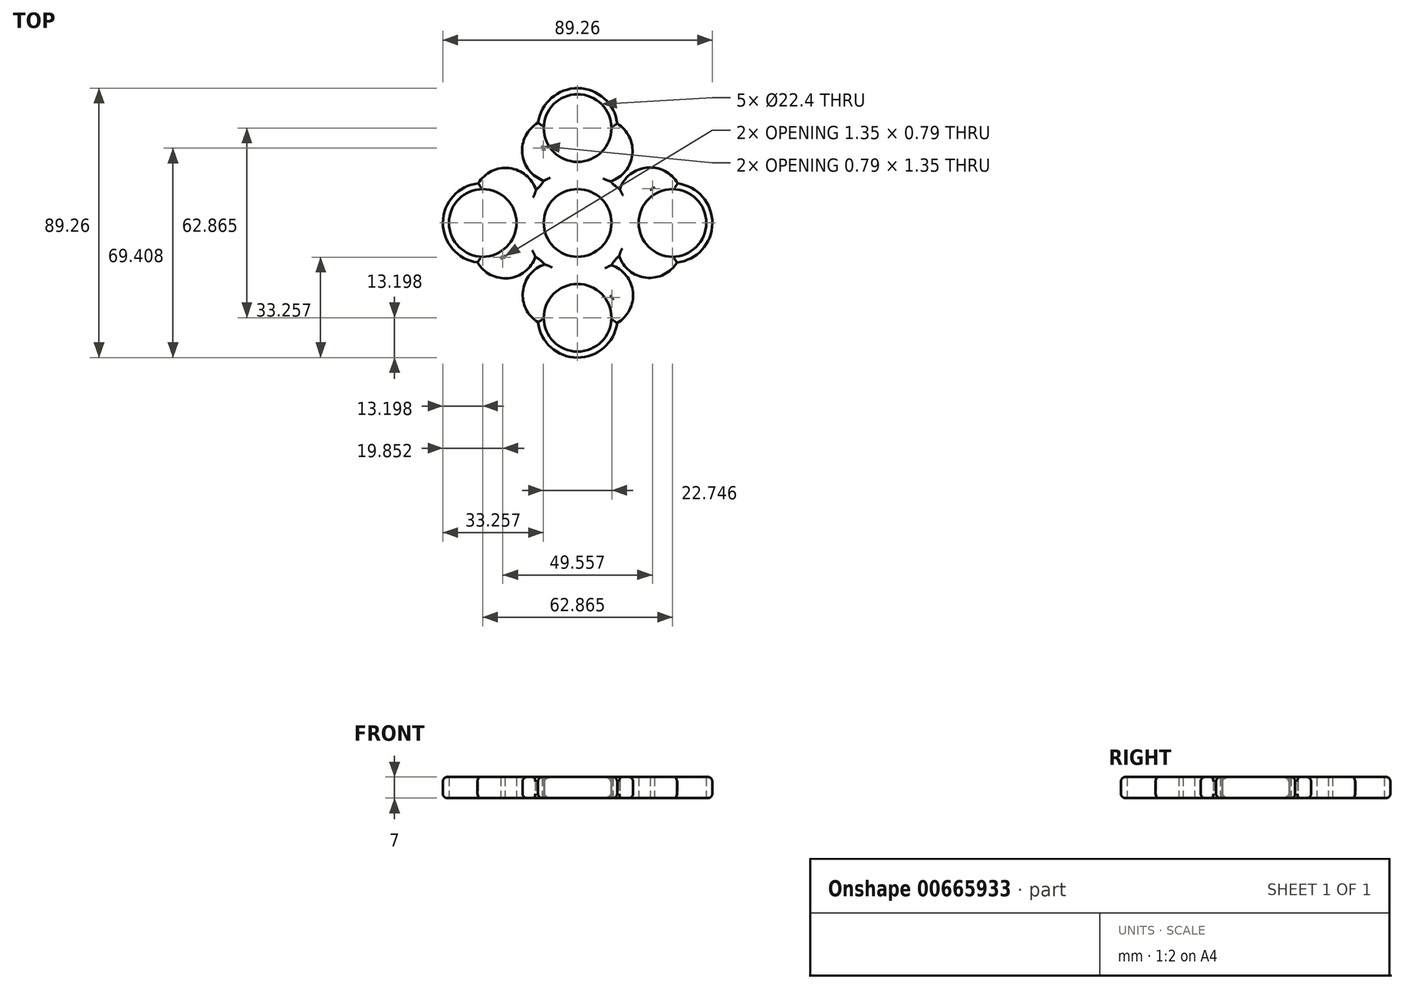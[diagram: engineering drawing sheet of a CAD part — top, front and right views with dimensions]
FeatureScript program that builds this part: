
annotation { "Feature Type Name" : "Feature", "Feature Type Description" : "" }
export const myFeature = defineFeature(function(context is Context, id is Id, definition is map)
    precondition{}
    {
        {
            var Q0;
            Q0=qCreatedBy(makeId("Top.planeOp"),FACE);
            var sketch = newSketch(context, id + "F0", { "sketchPlane" : qUnion([Q0])});
            skCircle(sketch, "E0", {"center": v(0, 0) * mm, "radius": 11.2 * mm});
            skCircle(sketch, "E1", {"center": v(0, 0) * mm, "radius": 13.2 * mm});
            skCircle(sketch, "E2", {"center": v(0, 31.43) * mm, "radius": 11.2 * mm});
            skCircle(sketch, "E3", {"center": v(0, 31.43) * mm, "radius": 13.2 * mm});
            skCircle(sketch, "E4.1.0", {"center": v(-31.43, 0) * mm, "radius": 13.2 * mm});
            skCircle(sketch, "E4.1.1", {"center": v(-31.43, 0) * mm, "radius": 11.2 * mm});
            skCircle(sketch, "E4.2.0", {"center": v(0, -31.43) * mm, "radius": 13.2 * mm});
            skCircle(sketch, "E4.2.1", {"center": v(0, -31.43) * mm, "radius": 11.2 * mm});
            skCircle(sketch, "E4.3.0", {"center": v(31.43, 0) * mm, "radius": 13.2 * mm});
            skCircle(sketch, "E4.3.1", {"center": v(31.43, 0) * mm, "radius": 11.2 * mm});
            skArc(sketch, "E5", {"start": v(-21.28, 8.44) * mm, "mid": v(-11.24, 14) * mm, "end": v(-11.77, 25.46) * mm});
            skArc(sketch, "E6.1.0", {"start": v(-8.44, -21.28) * mm, "mid": v(-14, -11.24) * mm, "end": v(-25.46, -11.77) * mm});
            skArc(sketch, "E6.2.0", {"start": v(21.28, -8.44) * mm, "mid": v(11.24, -14) * mm, "end": v(11.77, -25.46) * mm});
            skArc(sketch, "E6.3.0", {"start": v(8.44, 21.28) * mm, "mid": v(14, 11.24) * mm, "end": v(25.46, 11.77) * mm});
            skArc(sketch, "E7", {"start": v(-13.09, 33.16) * mm, "mid": v(-18.33, 22.98) * mm, "end": v(-11.24, 14) * mm});
            skArc(sketch, "E8.1.0", {"start": v(-33.16, -13.09) * mm, "mid": v(-22.98, -18.33) * mm, "end": v(-14, -11.24) * mm});
            skArc(sketch, "E8.2.0", {"start": v(13.09, -33.16) * mm, "mid": v(18.33, -22.98) * mm, "end": v(11.24, -14) * mm});
            skArc(sketch, "E8.3.0", {"start": v(33.16, 13.09) * mm, "mid": v(22.98, 18.33) * mm, "end": v(14, 11.24) * mm});
            skArc(sketch, "E9", {"start": v(10.95, 13.77) * mm, "mid": v(18.14, 22.65) * mm, "end": v(13.12, 32.91) * mm});
            skArc(sketch, "E10.1.0", {"start": v(-13.77, 10.95) * mm, "mid": v(-22.65, 18.14) * mm, "end": v(-32.91, 13.12) * mm});
            skArc(sketch, "E10.2.0", {"start": v(-10.95, -13.77) * mm, "mid": v(-18.14, -22.65) * mm, "end": v(-13.12, -32.91) * mm});
            skArc(sketch, "E10.3.0", {"start": v(13.77, -10.95) * mm, "mid": v(22.65, -18.14) * mm, "end": v(32.91, -13.12) * mm});
            skSolve(sketch);
        }
        {
            var Q0;
            Q0=makeQuery(id+"F0.imprint","IMPRINT",FACE,{"disambiguationData":[TD([[makeQuery(id+"F0.imprint","IMPRINT",EDGE,{"derivedFrom":sQuery(id+"F0.wireOp",EDGE,"E4.1.1")}),-1.0]])]});
            var Q1;
            {var subQ3=sQuery(id+"F0.wireOp",EDGE,"E10.1.0");Q1=makeQuery(id+"F0.imprint","IMPRINT",FACE,{"disambiguationData":[TD([[makeQuery(id+"F0.imprint","IMPRINT",EDGE,{"derivedFrom":subQ3}),1.0]])]});}
            var Q2;
            {var subQ3=sQuery(id+"F0.wireOp",EDGE,"E7");Q2=makeQuery(id+"F0.imprint","IMPRINT",FACE,{"disambiguationData":[TD([[makeQuery(id+"F0.imprint","IMPRINT",EDGE,{"derivedFrom":subQ3}),1.0]])]});}
            var Q3;
            {var subQ3=sQuery(id+"F0.wireOp",EDGE,"E9");Q3=makeQuery(id+"F0.imprint","IMPRINT",FACE,{"disambiguationData":[TD([[makeQuery(id+"F0.imprint","IMPRINT",EDGE,{"derivedFrom":subQ3}),1.0]])]});}
            var Q4;
            Q4=makeQuery(id+"F0.imprint","IMPRINT",FACE,{"disambiguationData":[TD([[makeQuery(id+"F0.imprint","IMPRINT",EDGE,{"derivedFrom":sQuery(id+"F0.wireOp",EDGE,"E2")}),-1.0]])]});
            var Q5;
            Q5=makeQuery(id+"F0.imprint","IMPRINT",FACE,{"disambiguationData":[TD([[makeQuery(id+"F0.imprint","IMPRINT",EDGE,{"derivedFrom":sQuery(id+"F0.wireOp",EDGE,"E4.3.1")}),-1.0]])]});
            var Q6;
            {var subQ3=sQuery(id+"F0.wireOp",EDGE,"E8.3.0");Q6=makeQuery(id+"F0.imprint","IMPRINT",FACE,{"disambiguationData":[TD([[makeQuery(id+"F0.imprint","IMPRINT",EDGE,{"derivedFrom":subQ3}),1.0]])]});}
            var Q7;
            {var subQ3=sQuery(id+"F0.wireOp",EDGE,"E10.3.0");Q7=makeQuery(id+"F0.imprint","IMPRINT",FACE,{"disambiguationData":[TD([[makeQuery(id+"F0.imprint","IMPRINT",EDGE,{"derivedFrom":subQ3}),1.0]])]});}
            var Q8;
            {var subQ3=sQuery(id+"F0.wireOp",EDGE,"E8.2.0");Q8=makeQuery(id+"F0.imprint","IMPRINT",FACE,{"disambiguationData":[TD([[makeQuery(id+"F0.imprint","IMPRINT",EDGE,{"derivedFrom":subQ3}),1.0]])]});}
            var Q9;
            Q9=makeQuery(id+"F0.imprint","IMPRINT",FACE,{"disambiguationData":[TD([[makeQuery(id+"F0.imprint","IMPRINT",EDGE,{"derivedFrom":sQuery(id+"F0.wireOp",EDGE,"E4.2.1")}),-1.0]])]});
            var Q10;
            Q10=makeQuery(id+"F0.imprint","IMPRINT",FACE,{"disambiguationData":[TD([[makeQuery(id+"F0.imprint","IMPRINT",EDGE,{"derivedFrom":sQuery(id+"F0.wireOp",EDGE,"E1")}),-1.0]])]});
            var Q11;
            {var subQ3=sQuery(id+"F0.wireOp",EDGE,"E10.2.0");Q11=makeQuery(id+"F0.imprint","IMPRINT",FACE,{"disambiguationData":[TD([[makeQuery(id+"F0.imprint","IMPRINT",EDGE,{"derivedFrom":subQ3}),1.0]])]});}
            var Q12;
            {var subQ3=sQuery(id+"F0.wireOp",EDGE,"E8.1.0");Q12=makeQuery(id+"F0.imprint","IMPRINT",FACE,{"disambiguationData":[TD([[makeQuery(id+"F0.imprint","IMPRINT",EDGE,{"derivedFrom":subQ3}),1.0]])]});}
            var Q13;
            Q13=makeQuery(id+"F0.imprint","IMPRINT",FACE,{"disambiguationData":[TD([[makeQuery(id+"F0.imprint","IMPRINT",EDGE,{"derivedFrom":sQuery(id+"F0.wireOp",EDGE,"E0")}),-1.0]])]});
            extrude(context, id + "F1", {"entities" : qUnion([Q0, Q1, Q2, Q3, Q4, Q5, Q6, Q7, Q8, Q9, Q10, Q11, Q12, Q13]), "depth" : 7 * mm, "offsetDistance" : 25 * mm});
        }
        {
            var Q0;
            Q0=makeQuery(id+"F1.opExtrude","CAP_EDGE",EDGE,{"disambiguationData":[OSD([sQuery(id+"F0.wireOp",EDGE,"E7")])],"isStart":false});
            var Q1;
            {var subQ0=sQuery(id+"F0.wireOp",EDGE,"E3");Q1=makeQuery(id+"F1.opExtrude","CAP_EDGE",EDGE,{"disambiguationData":[OSD([subQ0]),TDD([makeQuery(id+"F0.imprint","IMPRINT",EDGE,{"disambiguationData":[TD([[makeQuery(id+"F0.imprint","INTERSECT",VERTEX,{"derivedFrom":[subQ0,sQuery(id+"F0.wireOp",EDGE,"E7")]}),1.0]])],"derivedFrom":subQ0})])],"isStart":false});}
            var Q2;
            Q2=makeQuery(id+"F1.opExtrude","CAP_EDGE",EDGE,{"disambiguationData":[OSD([sQuery(id+"F0.wireOp",EDGE,"E9")])],"isStart":false});
            var Q3;
            Q3=makeQuery(id+"F1.opExtrude","CAP_EDGE",EDGE,{"disambiguationData":[OSD([sQuery(id+"F0.wireOp",EDGE,"E8.3.0")])],"isStart":false});
            var Q4;
            {var subQ0=sQuery(id+"F0.wireOp",EDGE,"E4.3.0");Q4=makeQuery(id+"F1.opExtrude","CAP_EDGE",EDGE,{"disambiguationData":[OSD([subQ0]),TDD([makeQuery(id+"F0.imprint","IMPRINT",EDGE,{"disambiguationData":[TD([[makeQuery(id+"F0.imprint","INTERSECT",VERTEX,{"derivedFrom":[subQ0,sQuery(id+"F0.wireOp",EDGE,"E8.3.0")]}),1.0]])],"derivedFrom":subQ0})])],"isStart":false});}
            var Q5;
            Q5=makeQuery(id+"F1.opExtrude","CAP_EDGE",EDGE,{"disambiguationData":[OSD([sQuery(id+"F0.wireOp",EDGE,"E10.3.0")])],"isStart":false});
            var Q6;
            Q6=makeQuery(id+"F1.opExtrude","CAP_EDGE",EDGE,{"disambiguationData":[OSD([sQuery(id+"F0.wireOp",EDGE,"E8.2.0")])],"isStart":false});
            var Q7;
            {var subQ0=sQuery(id+"F0.wireOp",EDGE,"E6.2.0");Q7=makeQuery(id+"F1.opExtrude","CAP_EDGE",EDGE,{"disambiguationData":[OSD([subQ0]),TDD([makeQuery(id+"F0.imprint","IMPRINT",EDGE,{"disambiguationData":[TD([[makeQuery(id+"F0.imprint","INTERSECT",VERTEX,{"derivedFrom":[subQ0,sQuery(id+"F0.wireOp",EDGE,"E8.2.0")]}),1.0]])],"derivedFrom":subQ0})])],"isStart":false});}
            var Q8;
            {var subQ0=sQuery(id+"F0.wireOp",EDGE,"E6.3.0");Q8=makeQuery(id+"F1.opExtrude","CAP_EDGE",EDGE,{"disambiguationData":[OSD([subQ0]),TDD([makeQuery(id+"F0.imprint","IMPRINT",EDGE,{"disambiguationData":[TD([[makeQuery(id+"F0.imprint","INTERSECT",VERTEX,{"derivedFrom":[subQ0,sQuery(id+"F0.wireOp",EDGE,"E8.3.0")]}),1.0]])],"derivedFrom":subQ0})])],"isStart":false});}
            var Q9;
            {var subQ0=sQuery(id+"F0.wireOp",EDGE,"E5");Q9=makeQuery(id+"F1.opExtrude","CAP_EDGE",EDGE,{"disambiguationData":[OSD([subQ0]),TDD([makeQuery(id+"F0.imprint","IMPRINT",EDGE,{"disambiguationData":[TD([[makeQuery(id+"F0.imprint","INTERSECT",VERTEX,{"derivedFrom":[subQ0,sQuery(id+"F0.wireOp",EDGE,"E7")]}),1.0]])],"derivedFrom":subQ0})])],"isStart":false});}
            var Q10;
            Q10=makeQuery(id+"F1.opExtrude","CAP_EDGE",EDGE,{"disambiguationData":[OSD([sQuery(id+"F0.wireOp",EDGE,"E10.1.0")])],"isStart":false});
            var Q11;
            {var subQ0=sQuery(id+"F0.wireOp",EDGE,"E4.1.0");Q11=makeQuery(id+"F1.opExtrude","CAP_EDGE",EDGE,{"disambiguationData":[OSD([subQ0]),TDD([makeQuery(id+"F0.imprint","IMPRINT",EDGE,{"disambiguationData":[TD([[makeQuery(id+"F0.imprint","INTERSECT",VERTEX,{"derivedFrom":[subQ0,sQuery(id+"F0.wireOp",EDGE,"E8.1.0")]}),1.0]])],"derivedFrom":subQ0})])],"isStart":false});}
            var Q12;
            Q12=makeQuery(id+"F1.opExtrude","CAP_EDGE",EDGE,{"disambiguationData":[OSD([sQuery(id+"F0.wireOp",EDGE,"E8.1.0")])],"isStart":false});
            var Q13;
            {var subQ0=sQuery(id+"F0.wireOp",EDGE,"E6.1.0");Q13=makeQuery(id+"F1.opExtrude","CAP_EDGE",EDGE,{"disambiguationData":[OSD([subQ0]),TDD([makeQuery(id+"F0.imprint","IMPRINT",EDGE,{"disambiguationData":[TD([[makeQuery(id+"F0.imprint","INTERSECT",VERTEX,{"derivedFrom":[subQ0,sQuery(id+"F0.wireOp",EDGE,"E8.1.0")]}),1.0]])],"derivedFrom":subQ0})])],"isStart":false});}
            var Q14;
            Q14=makeQuery(id+"F1.opExtrude","CAP_EDGE",EDGE,{"disambiguationData":[OSD([sQuery(id+"F0.wireOp",EDGE,"E10.2.0")])],"isStart":false});
            var Q15;
            {var subQ0=sQuery(id+"F0.wireOp",EDGE,"E4.2.0");Q15=makeQuery(id+"F1.opExtrude","CAP_EDGE",EDGE,{"disambiguationData":[OSD([subQ0]),TDD([makeQuery(id+"F0.imprint","IMPRINT",EDGE,{"disambiguationData":[TD([[makeQuery(id+"F0.imprint","INTERSECT",VERTEX,{"derivedFrom":[subQ0,sQuery(id+"F0.wireOp",EDGE,"E8.2.0")]}),1.0]])],"derivedFrom":subQ0})])],"isStart":false});}
            fillet(context, id + "F2", {"entities" : qUnion([Q0, Q1, Q2, Q3, Q4, Q5, Q6, Q7, Q8, Q9, Q10, Q11, Q12, Q13, Q14, Q15]), "radius" : 1.5 * mm, "tangentPropagation" : true, "allowEdgeOverflow" : false});
        }
        {
            var Q0;
            Q0=makeQuery(id+"F1.opExtrude","CAP_EDGE",EDGE,{"disambiguationData":[OSD([sQuery(id+"F0.wireOp",EDGE,"E8.1.0")])],"isStart":true});
            var Q1;
            {var subQ0=sQuery(id+"F0.wireOp",EDGE,"E4.1.0");Q1=makeQuery(id+"F1.opExtrude","CAP_EDGE",EDGE,{"disambiguationData":[OSD([subQ0]),TDD([makeQuery(id+"F0.imprint","IMPRINT",EDGE,{"disambiguationData":[TD([[makeQuery(id+"F0.imprint","INTERSECT",VERTEX,{"derivedFrom":[subQ0,sQuery(id+"F0.wireOp",EDGE,"E8.1.0")]}),1.0]])],"derivedFrom":subQ0})])],"isStart":true});}
            var Q2;
            Q2=makeQuery(id+"F1.opExtrude","CAP_EDGE",EDGE,{"disambiguationData":[OSD([sQuery(id+"F0.wireOp",EDGE,"E10.1.0")])],"isStart":true});
            var Q3;
            {var subQ0=sQuery(id+"F0.wireOp",EDGE,"E5");Q3=makeQuery(id+"F1.opExtrude","CAP_EDGE",EDGE,{"disambiguationData":[OSD([subQ0]),TDD([makeQuery(id+"F0.imprint","IMPRINT",EDGE,{"disambiguationData":[TD([[makeQuery(id+"F0.imprint","INTERSECT",VERTEX,{"derivedFrom":[subQ0,sQuery(id+"F0.wireOp",EDGE,"E7")]}),1.0]])],"derivedFrom":subQ0})])],"isStart":true});}
            var Q4;
            Q4=makeQuery(id+"F1.opExtrude","CAP_EDGE",EDGE,{"disambiguationData":[OSD([sQuery(id+"F0.wireOp",EDGE,"E7")])],"isStart":true});
            var Q5;
            {var subQ0=sQuery(id+"F0.wireOp",EDGE,"E3");Q5=makeQuery(id+"F1.opExtrude","CAP_EDGE",EDGE,{"disambiguationData":[OSD([subQ0]),TDD([makeQuery(id+"F0.imprint","IMPRINT",EDGE,{"disambiguationData":[TD([[makeQuery(id+"F0.imprint","INTERSECT",VERTEX,{"derivedFrom":[subQ0,sQuery(id+"F0.wireOp",EDGE,"E7")]}),1.0]])],"derivedFrom":subQ0})])],"isStart":true});}
            var Q6;
            Q6=makeQuery(id+"F1.opExtrude","CAP_EDGE",EDGE,{"disambiguationData":[OSD([sQuery(id+"F0.wireOp",EDGE,"E9")])],"isStart":true});
            var Q7;
            {var subQ0=sQuery(id+"F0.wireOp",EDGE,"E6.3.0");Q7=makeQuery(id+"F1.opExtrude","CAP_EDGE",EDGE,{"disambiguationData":[OSD([subQ0]),TDD([makeQuery(id+"F0.imprint","IMPRINT",EDGE,{"disambiguationData":[TD([[makeQuery(id+"F0.imprint","INTERSECT",VERTEX,{"derivedFrom":[subQ0,sQuery(id+"F0.wireOp",EDGE,"E8.3.0")]}),1.0]])],"derivedFrom":subQ0})])],"isStart":true});}
            var Q8;
            Q8=makeQuery(id+"F1.opExtrude","CAP_EDGE",EDGE,{"disambiguationData":[OSD([sQuery(id+"F0.wireOp",EDGE,"E8.3.0")])],"isStart":true});
            var Q9;
            {var subQ0=sQuery(id+"F0.wireOp",EDGE,"E4.3.0");Q9=makeQuery(id+"F1.opExtrude","CAP_EDGE",EDGE,{"disambiguationData":[OSD([subQ0]),TDD([makeQuery(id+"F0.imprint","IMPRINT",EDGE,{"disambiguationData":[TD([[makeQuery(id+"F0.imprint","INTERSECT",VERTEX,{"derivedFrom":[subQ0,sQuery(id+"F0.wireOp",EDGE,"E8.3.0")]}),1.0]])],"derivedFrom":subQ0})])],"isStart":true});}
            var Q10;
            Q10=makeQuery(id+"F1.opExtrude","CAP_EDGE",EDGE,{"disambiguationData":[OSD([sQuery(id+"F0.wireOp",EDGE,"E10.3.0")])],"isStart":true});
            var Q11;
            Q11=makeQuery(id+"F1.opExtrude","CAP_EDGE",EDGE,{"disambiguationData":[OSD([sQuery(id+"F0.wireOp",EDGE,"E8.2.0")])],"isStart":true});
            var Q12;
            {var subQ0=sQuery(id+"F0.wireOp",EDGE,"E6.2.0");Q12=makeQuery(id+"F1.opExtrude","CAP_EDGE",EDGE,{"disambiguationData":[OSD([subQ0]),TDD([makeQuery(id+"F0.imprint","IMPRINT",EDGE,{"disambiguationData":[TD([[makeQuery(id+"F0.imprint","INTERSECT",VERTEX,{"derivedFrom":[subQ0,sQuery(id+"F0.wireOp",EDGE,"E8.2.0")]}),1.0]])],"derivedFrom":subQ0})])],"isStart":true});}
            var Q13;
            {var subQ0=sQuery(id+"F0.wireOp",EDGE,"E4.2.0");Q13=makeQuery(id+"F1.opExtrude","CAP_EDGE",EDGE,{"disambiguationData":[OSD([subQ0]),TDD([makeQuery(id+"F0.imprint","IMPRINT",EDGE,{"disambiguationData":[TD([[makeQuery(id+"F0.imprint","INTERSECT",VERTEX,{"derivedFrom":[subQ0,sQuery(id+"F0.wireOp",EDGE,"E8.2.0")]}),1.0]])],"derivedFrom":subQ0})])],"isStart":true});}
            var Q14;
            Q14=makeQuery(id+"F1.opExtrude","CAP_EDGE",EDGE,{"disambiguationData":[OSD([sQuery(id+"F0.wireOp",EDGE,"E10.2.0")])],"isStart":true});
            var Q15;
            {var subQ0=sQuery(id+"F0.wireOp",EDGE,"E6.1.0");Q15=makeQuery(id+"F1.opExtrude","CAP_EDGE",EDGE,{"disambiguationData":[OSD([subQ0]),TDD([makeQuery(id+"F0.imprint","IMPRINT",EDGE,{"disambiguationData":[TD([[makeQuery(id+"F0.imprint","INTERSECT",VERTEX,{"derivedFrom":[subQ0,sQuery(id+"F0.wireOp",EDGE,"E8.1.0")]}),1.0]])],"derivedFrom":subQ0})])],"isStart":true});}
            fillet(context, id + "F3", {"entities" : qUnion([Q0, Q1, Q2, Q3, Q4, Q5, Q6, Q7, Q8, Q9, Q10, Q11, Q12, Q13, Q14, Q15]), "radius" : 1.5 * mm, "tangentPropagation" : true, "allowEdgeOverflow" : false});
        }
    });
